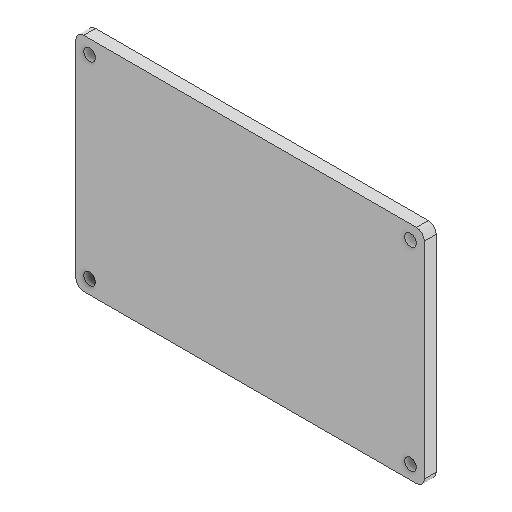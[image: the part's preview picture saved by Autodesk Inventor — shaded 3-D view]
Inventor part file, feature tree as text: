
AUTODESK INVENTOR PART (.ipt)
format: ipt  version: 2025.2 (Build 292293000, 293)  size: 102,912 bytes
history: native  units: mm
features: sketch x2, extrude x1, fillet x1, hole x1
ambient origin geometry x8: Origin, YZ Plane, XZ Plane, XY Plane, X Axis, Y Axis, Z Axis, Center Point
bodies: Solid1 (feature_tree)
feature tree (5):
  extrude  "Extrusion1"  Depth=56.0mm
  fillet  "Fillet1"  Radius=3.0mm
  hole  "Hole1"  [1 undecoded]
  sketch  "Sketch1"  dims[d0=88.0mm d1=56.0mm d2=3.0mm d3=0.0mm]
  sketch  "Sketch2"  dims[d4=2.0mm d5=3.0mm d6=6.0mm d7=4.0mm d8=2.0mm d9=90.0deg d10=8.0mm d11=20.594885mm d12=81.0mm d13=49.0mm]
note: 1 required parameter value undecoded (feature->parameter linkage not recoverable at this tier; creation-order binding heuristic only, values carry confidence <= 0.55)
